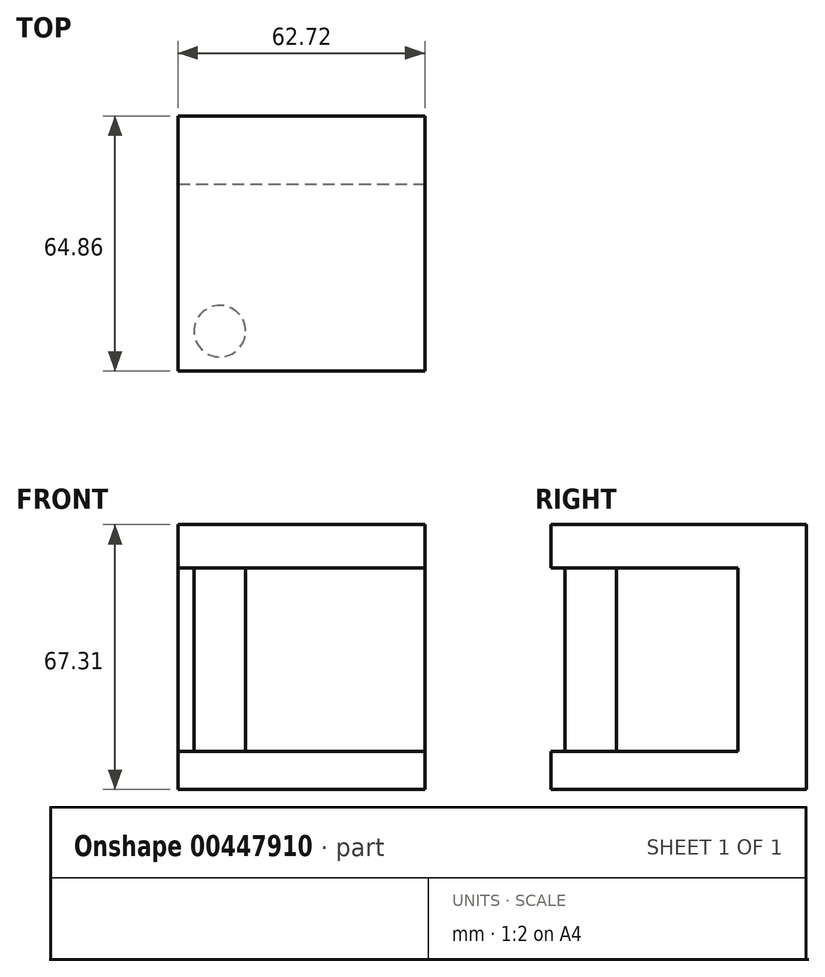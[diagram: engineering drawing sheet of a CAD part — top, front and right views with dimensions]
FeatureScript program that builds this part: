
annotation { "Feature Type Name" : "Feature", "Feature Type Description" : "" }
export const myFeature = defineFeature(function(context is Context, id is Id, definition is map)
    precondition{}
    {
        {
            var Q0;
            Q0=qCreatedBy(makeId("Top.planeOp"),FACE);
            var sketch = newSketch(context, id + "F0", { "sketchPlane" : qUnion([Q0])});
            skLineSegment(sketch, "E0.bottom", {"start": v(-31.65, 31.46) * mm, "end": v(31.07, 31.46) * mm});
            skLineSegment(sketch, "E0.top", {"start": v(-31.65, -33.4) * mm, "end": v(31.07, -33.4) * mm});
            skLineSegment(sketch, "E0.left", {"start": v(-31.65, 31.46) * mm, "end": v(-31.65, -33.4) * mm});
            skLineSegment(sketch, "E0.right", {"start": v(31.07, 31.46) * mm, "end": v(31.07, -33.4) * mm});
            skSolve(sketch);
        }
        {
            var Q0;
            Q0=makeQuery(id+"F0.imprint","IMPRINT",FACE,{"disambiguationData":[TD([[makeQuery(id+"F0.imprint","IMPRINT",EDGE,{"derivedFrom":sQuery(id+"F0.wireOp",EDGE,"E0.bottom")}),-1.0]])]});
            extrude(context, id + "F1", {"entities" : qUnion([Q0]), "depth" : 67.3 * mm});
        }
        {
            var Q0;
            Q0=makeQuery(id+"F1.opExtrude","SWEPT_FACE",FACE,{"disambiguationData":[OSD([sQuery(id+"F0.wireOp",EDGE,"E0.right")])]});
            var sketch = newSketch(context, id + "F2", { "sketchPlane" : qUnion([Q0])});
            skLineSegment(sketch, "E1.bottom", {"start": v(-33.4, 56.32) * mm, "end": v(14.18, 56.32) * mm});
            skLineSegment(sketch, "E1.top", {"start": v(-33.4, 9.7) * mm, "end": v(14.18, 9.7) * mm});
            skLineSegment(sketch, "E1.left", {"start": v(-33.4, 56.32) * mm, "end": v(-33.4, 9.7) * mm});
            skLineSegment(sketch, "E1.right", {"start": v(14.18, 56.32) * mm, "end": v(14.18, 9.7) * mm});
            skSolve(sketch);
        }
        {
            var Q0;
            Q0=makeQuery(id+"F2.imprint","IMPRINT",FACE,{"disambiguationData":[TD([[makeQuery(id+"F2.imprint","IMPRINT",EDGE,{"derivedFrom":sQuery(id+"F2.wireOp",EDGE,"E1.bottom")}),-1.0]])]});
            extrude(context, id + "F3", {"entities" : qUnion([Q0]), "operationType" : NewBodyOperationType.REMOVE, "oppositeDirection" : true, "depth" : 72.64 * mm});
        }
        {
            var Q0;
            Q0=makeQuery(id+"F3.boolean.opBoolean","COPY",FACE,{"derivedFrom":makeQuery(id+"F3.opExtrude","SWEPT_FACE",FACE,{"disambiguationData":[OSD([sQuery(id+"F2.wireOp",EDGE,"E1.top")])]})});
            var sketch = newSketch(context, id + "F4", { "sketchPlane" : qUnion([Q0])});
            skCircle(sketch, "E2", {"center": v(-21.05, -23.22) * mm, "radius": 6.54 * mm});
            skSolve(sketch);
        }
        {
            var Q0;
            Q0=makeQuery(id+"F4.imprint","IMPRINT",FACE,{"disambiguationData":[TD([[makeQuery(id+"F4.imprint","IMPRINT",EDGE,{"derivedFrom":sQuery(id+"F4.wireOp",EDGE,"E2")}),1.0]])]});
            extrude(context, id + "F5", {"entities" : qUnion([Q0]), "operationType" : NewBodyOperationType.ADD, "depth" : 52.07 * mm});
        }
    });
